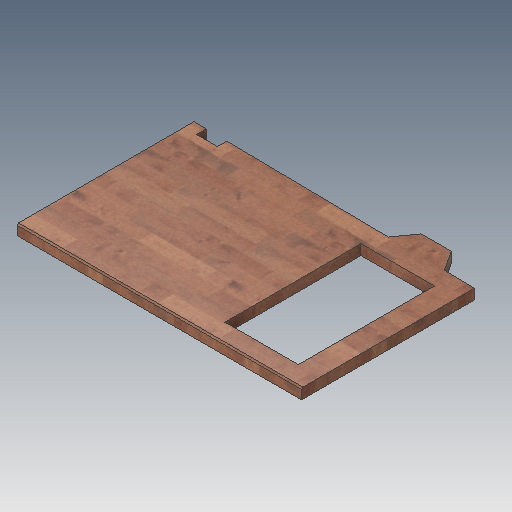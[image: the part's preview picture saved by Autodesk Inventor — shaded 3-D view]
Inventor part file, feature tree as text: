
AUTODESK INVENTOR PART (.ipt)
format: ipt  version: 2018 (Build 220112000, 112)  size: 250,880 bytes
history: native  units: mm
features: extrude x4, sketch x3, chamfer x1, projected_geometry x1
ambient origin geometry x8: Origin, YZ Plane, XZ Plane, XY Plane, X Axis, Y Axis, Z Axis, Center Point
bodies: Solid1 (feature_tree)
feature tree (9):
  extrude  "Extrusion1"  Depth=38.0mm TaperAngle=0.0deg
  chamfer  "Chamfer1"  Distance=5.0mm Angle=45.0deg
  extrude  "Extrusion3"  Depth=270.0mm
  extrude  "Extrusion4"  Depth=710.0mm TaperAngle=0.0deg
  extrude  "Extrusion5"  Depth=68.282467mm
  sketch  "Sketch3"  dims[d2=635.0mm d5=38.0mm d6=0.0mm d7=5.0mm d8=2.0mm d9=45.0deg]
  projected_geometry  "Projected Loop2"
  sketch  "Sketch4"  dims[d19=10.0mm d20=0.0mm d21=270.0mm]
  sketch  "Sketch5"  dims[d22=500.0mm d23=10.0mm d24=0.0mm d25=68.282467mm d26=1045.0mm d27=15.84759mm d28=710.0mm d29=10.0mm d30=0.0mm d31=215.0mm d32=215.0mm]
